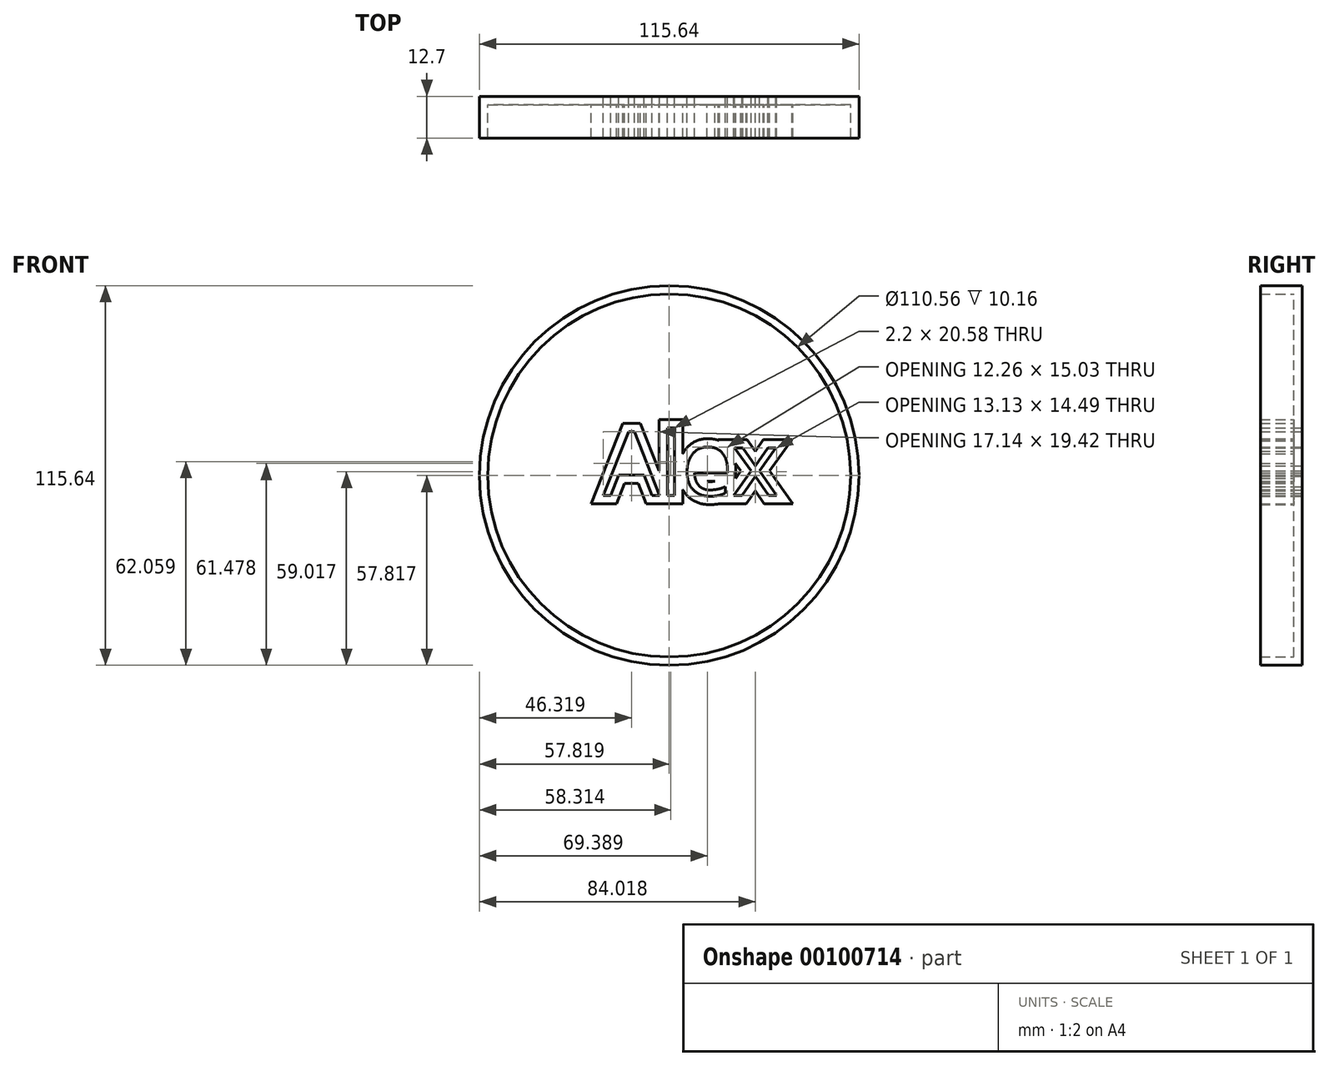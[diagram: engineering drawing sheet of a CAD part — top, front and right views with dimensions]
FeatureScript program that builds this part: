
annotation { "Feature Type Name" : "Feature", "Feature Type Description" : "" }
export const myFeature = defineFeature(function(context is Context, id is Id, definition is map)
    precondition{}
    {
        {
            var Q0;
            Q0=qCreatedBy(makeId("Front.planeOp"),FACE);
            var sketch = newSketch(context, id + "F0", { "sketchPlane" : qUnion([Q0])});
            skCircle(sketch, "E0", {"center": v(-131.85, 44.45) * mm, "radius": 57.82 * mm});
            skText(sketch, "E1", { "text": "Alex", "fontName": "OpenSans-Regular.ttf"});
            const initialGuessF0  = {"E1": [-0.15192, 0.0384, 1, 0, 0.0195]};
            skSetInitialGuess(sketch, initialGuessF0);
            skSolve(sketch);
        }
        {
            var Q0;
            Q0=makeQuery(id+"F0.imprint","IMPRINT",FACE,{"disambiguationData":[TD([[makeQuery(id+"F0.imprint","IMPRINT",EDGE,{"derivedFrom":sQuery(id+"F0.wireOp",EDGE,"E0")}),1.0]])]});
            var Q1;
            Q1 = qSketchRegion(id + "F0", true);
            extrude(context, id + "F1", {"entities" : qUnion([Q0, Q1]), "depth" : 12.7 * mm});
        }
        {
            var Q0;
            Q0=makeQuery(id+"F1.opExtrude","CAP_FACE",FACE,{"disambiguationData":[OSD([sQuery(id+"F0.wireOp",EDGE,"E0"),sQuery(id+"F0.wireOp",EDGE,"E1.sketch_text.stroke-0"),sQuery(id+"F0.wireOp",EDGE,"E1.sketch_text.stroke-1"),sQuery(id+"F0.wireOp",EDGE,"E1.sketch_text.stroke-2"),sQuery(id+"F0.wireOp",EDGE,"E1.sketch_text.stroke-3"),sQuery(id+"F0.wireOp",EDGE,"E1.sketch_text.stroke-4"),sQuery(id+"F0.wireOp",EDGE,"E1.sketch_text.stroke-5"),sQuery(id+"F0.wireOp",EDGE,"E1.sketch_text.stroke-6"),sQuery(id+"F0.wireOp",EDGE,"E1.sketch_text.stroke-7"),sQuery(id+"F0.wireOp",EDGE,"E1.sketch_text.stroke-13"),sQuery(id+"F0.wireOp",EDGE,"E1.sketch_text.stroke-14"),sQuery(id+"F0.wireOp",EDGE,"E1.sketch_text.stroke-15"),sQuery(id+"F0.wireOp",EDGE,"E1.sketch_text.stroke-16"),sQuery(id+"F0.wireOp",EDGE,"E1.sketch_text.stroke-17"),sQuery(id+"F0.wireOp",EDGE,"E1.sketch_text.stroke-18"),sQuery(id+"F0.wireOp",EDGE,"E1.sketch_text.stroke-19"),sQuery(id+"F0.wireOp",EDGE,"E1.sketch_text.stroke-20"),sQuery(id+"F0.wireOp",EDGE,"E1.sketch_text.stroke-21"),sQuery(id+"F0.wireOp",EDGE,"E1.sketch_text.stroke-22"),sQuery(id+"F0.wireOp",EDGE,"E1.sketch_text.stroke-23"),sQuery(id+"F0.wireOp",EDGE,"E1.sketch_text.stroke-24"),sQuery(id+"F0.wireOp",EDGE,"E1.sketch_text.stroke-25"),sQuery(id+"F0.wireOp",EDGE,"E1.sketch_text.stroke-26"),sQuery(id+"F0.wireOp",EDGE,"E1.sketch_text.stroke-27"),sQuery(id+"F0.wireOp",EDGE,"E1.sketch_text.stroke-28"),sQuery(id+"F0.wireOp",EDGE,"E1.sketch_text.stroke-29"),sQuery(id+"F0.wireOp",EDGE,"E1.sketch_text.stroke-30"),sQuery(id+"F0.wireOp",EDGE,"E1.sketch_text.stroke-36"),sQuery(id+"F0.wireOp",EDGE,"E1.sketch_text.stroke-37"),sQuery(id+"F0.wireOp",EDGE,"E1.sketch_text.stroke-38"),sQuery(id+"F0.wireOp",EDGE,"E1.sketch_text.stroke-39"),sQuery(id+"F0.wireOp",EDGE,"E1.sketch_text.stroke-40"),sQuery(id+"F0.wireOp",EDGE,"E1.sketch_text.stroke-41"),sQuery(id+"F0.wireOp",EDGE,"E1.sketch_text.stroke-42"),sQuery(id+"F0.wireOp",EDGE,"E1.sketch_text.stroke-43"),sQuery(id+"F0.wireOp",EDGE,"E1.sketch_text.stroke-44"),sQuery(id+"F0.wireOp",EDGE,"E1.sketch_text.stroke-45"),sQuery(id+"F0.wireOp",EDGE,"E1.sketch_text.stroke-46"),sQuery(id+"F0.wireOp",EDGE,"E1.sketch_text.stroke-47")])],"isStart":false});
            shell(context, id + "F2", {"entities" : qUnion([Q0]), "thickness" : 2.54 * mm});
        }
    });
